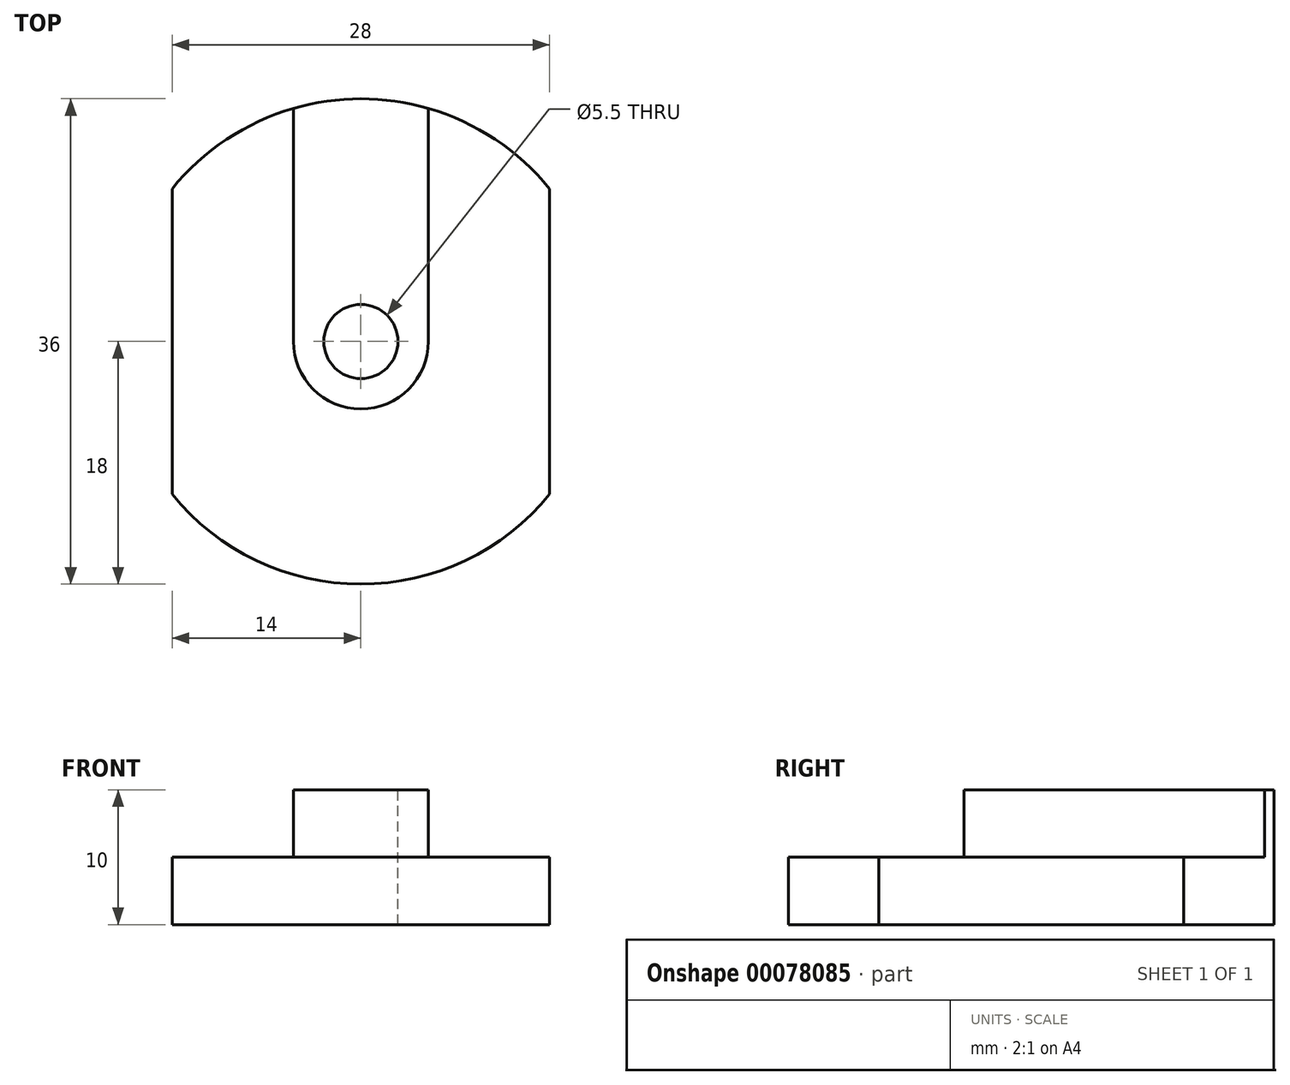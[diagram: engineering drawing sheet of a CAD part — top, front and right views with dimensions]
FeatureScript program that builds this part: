
annotation { "Feature Type Name" : "Feature", "Feature Type Description" : "" }
export const myFeature = defineFeature(function(context is Context, id is Id, definition is map)
    precondition{}
    {
        {
            var Q0;
            Q0=qCreatedBy(makeId("Top.planeOp"),FACE);
            var sketch = newSketch(context, id + "F0", { "sketchPlane" : qUnion([Q0])});
            skArc(sketch, "E0", {"start": v(-14, -11.31) * mm, "mid": v(0, -18) * mm, "end": v(14, -11.31) * mm});
            skLineSegment(sketch, "E1", {"start": v(-14, -11.31) * mm, "end": v(-14, 11.31) * mm});
            skLineSegment(sketch, "E2.MirrorCS", {"start": v(14, -11.31) * mm, "end": v(14, 11.31) * mm});
            skArc(sketch, "E3.trimOffspring", {"start": v(14, 11.31) * mm, "mid": v(0, 18) * mm, "end": v(-14, 11.31) * mm});
            skPoint(sketch, "E4.orphan", {"position": v(-14, 27.96) * mm});
            skPoint(sketch, "E5.orphan", {"position": v(14, 27.96) * mm});
            skSolve(sketch);
        }
        {
            var Q0;
            Q0=makeQuery(id+"F0.imprint","IMPRINT",FACE,{"disambiguationData":[TD([[makeQuery(id+"F0.imprint","IMPRINT",EDGE,{"derivedFrom":sQuery(id+"F0.wireOp",EDGE,"E0")}),1.0]])]});
            extrude(context, id + "F1", {"entities" : qUnion([Q0]), "depth" : 5 * mm});
        }
        {
            var Q0;
            Q0=makeQuery(id+"F1.opExtrude","CAP_FACE",FACE,{"disambiguationData":[OSD([sQuery(id+"F0.wireOp",EDGE,"E0"),sQuery(id+"F0.wireOp",EDGE,"E1"),sQuery(id+"F0.wireOp",EDGE,"E2.MirrorCS"),sQuery(id+"F0.wireOp",EDGE,"E3.trimOffspring")])],"isStart":false});
            var sketch = newSketch(context, id + "F2", { "sketchPlane" : qUnion([Q0])});
            skArc(sketch, "E6", {"start": v(-5, 0) * mm, "mid": v(0, -5) * mm, "end": v(5, 0) * mm});
            skLineSegment(sketch, "E7", {"start": v(-5, 0) * mm, "end": v(-5, 17.3) * mm});
            skPoint(sketch, "E7.startSnap0", {"position": v(-14, 0) * mm});
            skLineSegment(sketch, "E8", {"start": v(5, 0) * mm, "end": v(5, 17.3) * mm});
            skArc(sketch, "E9", {"start": v(5, 17.3) * mm, "mid": v(0, 18) * mm, "end": v(-5, 17.3) * mm});
            skSolve(sketch);
        }
        {
            var Q0;
            Q0=makeQuery(id+"F2.imprint","IMPRINT",FACE,{"disambiguationData":[TD([[makeQuery(id+"F2.imprint","IMPRINT",EDGE,{"derivedFrom":sQuery(id+"F2.wireOp",EDGE,"E6")}),1.0]])]});
            extrude(context, id + "F3", {"entities" : qUnion([Q0]), "operationType" : NewBodyOperationType.ADD, "depth" : 5 * mm});
        }
        {
            var Q0;
            Q0=makeQuery(id+"F1.opExtrude","CAP_FACE",FACE,{"disambiguationData":[OSD([sQuery(id+"F0.wireOp",EDGE,"E0"),sQuery(id+"F0.wireOp",EDGE,"E1"),sQuery(id+"F0.wireOp",EDGE,"E2.MirrorCS"),sQuery(id+"F0.wireOp",EDGE,"E3.trimOffspring")])],"isStart":true});
            var sketch = newSketch(context, id + "F4", { "sketchPlane" : qUnion([Q0])});
            skPoint(sketch, "E10", {"position": v(0, 0) * mm});
            skSolve(sketch);
        }
        {
            var Q0;
            Q0=sQuery(id+"F4.wireOp",VERTEX,"E10");
            var Q1;
            Q1=makeQuery(id+"F1.opExtrude","SWEPT_BODY",BODY,{"disambiguationData":[OSD([sQuery(id+"F0.wireOp",EDGE,"E0"),sQuery(id+"F0.wireOp",EDGE,"E1"),sQuery(id+"F0.wireOp",EDGE,"E2.MirrorCS"),sQuery(id+"F0.wireOp",EDGE,"E3.trimOffspring")])]});
            hole(context, id + "F5", {"style" : HoleStyle.SIMPLE, "endStyle" : HoleEndStyle.THROUGH, "standardTappedOrClearance" : lookupTablePath({ "standard" : "ISO", "fit" : "Normal", "size" : "M5", "type" : "Clearance" }), "standardBlindInLast" : lookupTablePath({ "fit" : "Standard", "standard" : "ISO", "size" : "M5", "type" : "Clearance" }), "holeDiameter" : 5.5 * mm, "locations" : qUnion([Q0]), "scope" : qUnion([Q1]), "isTappedThrough" : true});
        }
    });
